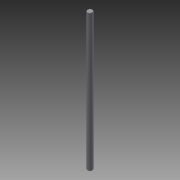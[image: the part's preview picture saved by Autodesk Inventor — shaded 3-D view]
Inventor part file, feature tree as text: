
AUTODESK INVENTOR PART (.ipt)
format: ipt  version: 2015 (Build 190159000, 159)  size: 68,608 bytes
history: native  units: in
note: dims shown in document units (in); Inventor stores cm internally (conversion verified against a paired STEP export)
features: extrude x1, chamfer x1, sketch x1
ambient origin geometry x8: Origin, YZ Plane, XZ Plane, XY Plane, X Axis, Y Axis, Z Axis, Center Point
bodies: Solid1 (feature_tree)
feature tree (3):
  extrude  "Extrusion1"  Depth=17.0in TaperAngle=0.0deg
  chamfer  "Chamfer1"  Distance=0.0394in Angle=45.0deg
  sketch  "Sketch1"  dims[d0=0.625in d1=17.0in d2=0.0in d3=0.0394in d4=0.0787in d5=45.0deg]
